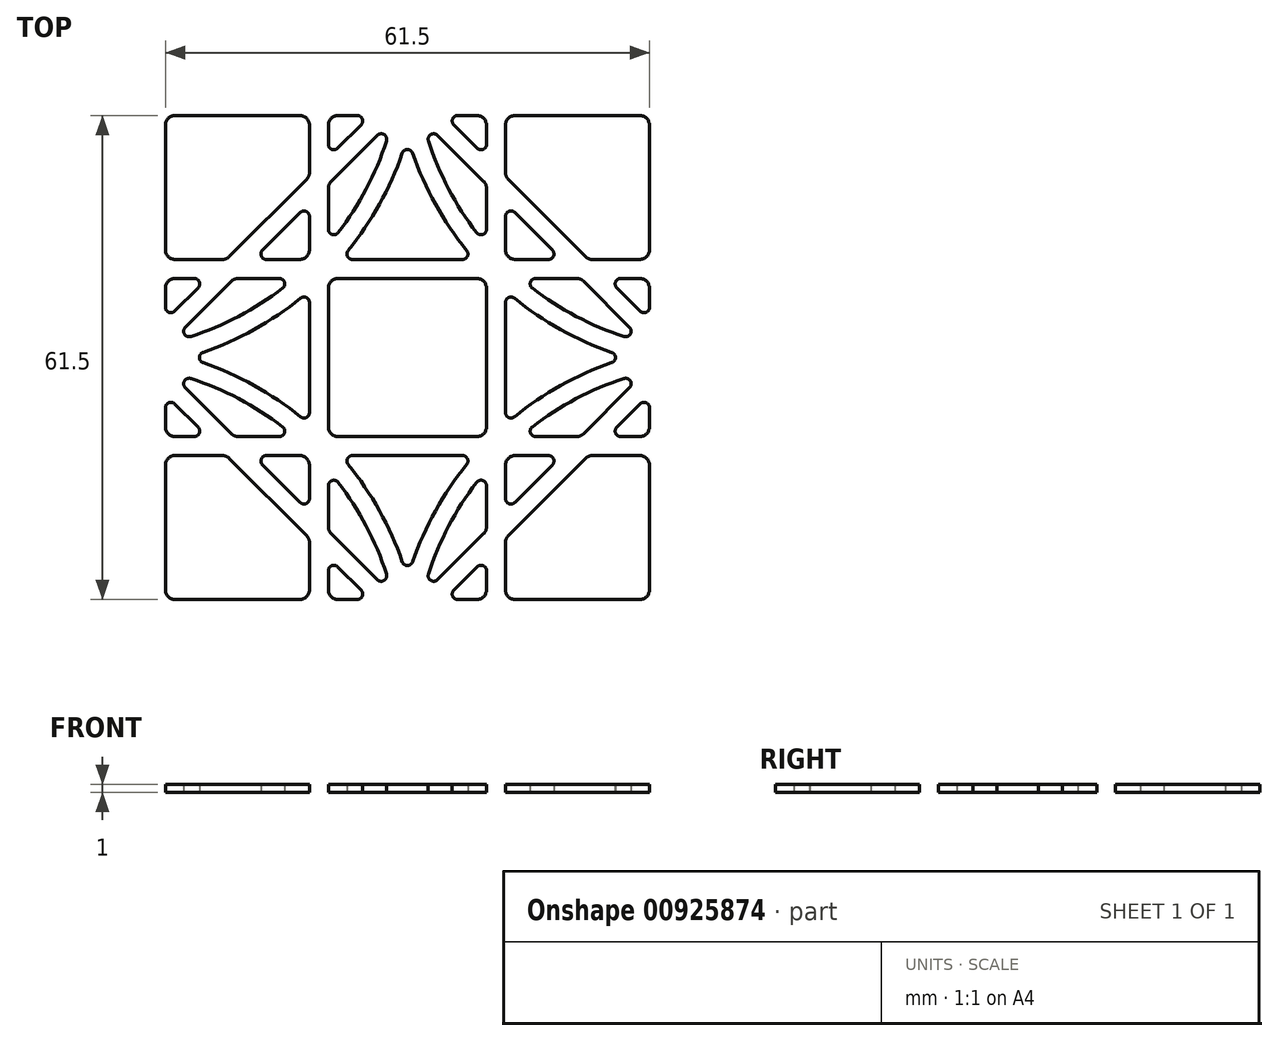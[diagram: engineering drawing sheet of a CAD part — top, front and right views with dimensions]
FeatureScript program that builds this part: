
annotation { "Feature Type Name" : "Feature", "Feature Type Description" : "" }
export const myFeature = defineFeature(function(context is Context, id is Id, definition is map)
    precondition{}
    {
        {
            var Q0;
            Q0=qCreatedBy(makeId("Top.planeOp"),FACE);
            var sketch = newSketch(context, id + "F0", { "sketchPlane" : qUnion([Q0])});
            skLineSegment(sketch, "E0.bottom", {"start": v(33.75, 33.75) * mm, "end": v(-33.75, 33.75) * mm, "construction": true});
            skLineSegment(sketch, "E0.top", {"start": v(33.75, -33.75) * mm, "end": v(-33.75, -33.75) * mm, "construction": true});
            skLineSegment(sketch, "E0.left", {"start": v(33.75, 33.75) * mm, "end": v(33.75, -33.75) * mm, "construction": true});
            skLineSegment(sketch, "E0.right", {"start": v(-33.75, 33.75) * mm, "end": v(-33.75, -33.75) * mm, "construction": true});
            skPoint(sketch, "E0.middle", {"position": v(0, 0) * mm});
            skLineSegment(sketch, "E1", {"start": v(-11.25, 33.75) * mm, "end": v(-11.25, -33.75) * mm, "construction": true});
            skLineSegment(sketch, "E2.1.0", {"start": v(-33.75, -11.25) * mm, "end": v(33.75, -11.25) * mm, "construction": true});
            skLineSegment(sketch, "E2.2.0", {"start": v(11.25, -33.75) * mm, "end": v(11.25, 33.75) * mm, "construction": true});
            skLineSegment(sketch, "E2.3.0", {"start": v(33.75, 11.25) * mm, "end": v(-33.75, 11.25) * mm, "construction": true});
            skArc(sketch, "E3", {"start": v(0, -33.75) * mm, "mid": v(-11.25, -11.25) * mm, "end": v(-33.75, 0) * mm, "construction": true});
            skPoint(sketch, "E4", {"position": v(-11.25, -11.25) * mm});
            skLineSegment(sketch, "E5", {"start": v(-33.75, 0) * mm, "end": v(0, -33.75) * mm, "construction": true});
            skArc(sketch, "E6", {"start": v(33.75, 0) * mm, "mid": v(11.25, -11.25) * mm, "end": v(0, -33.75) * mm, "construction": true});
            skPoint(sketch, "E7", {"position": v(11.25, -11.25) * mm});
            skLineSegment(sketch, "E8.bottom", {"start": v(-29.5, -12.45) * mm, "end": v(-23.51, -12.45) * mm});
            skLineSegment(sketch, "E8.top", {"start": v(-29.5, -30.75) * mm, "end": v(-13.7, -30.75) * mm});
            skLineSegment(sketch, "E8.left", {"start": v(-30.75, -13.7) * mm, "end": v(-30.75, -29.5) * mm});
            skLineSegment(sketch, "E8.right", {"start": v(-12.45, -13.7) * mm, "end": v(-12.45, -17.91) * mm});
            skLineSegment(sketch, "E9.bottom", {"start": v(-6.99, -12.45) * mm, "end": v(6.99, -12.45) * mm});
            skLineSegment(sketch, "E9.top", {"start": v(-8.8, -30.75) * mm, "end": v(-6.39, -30.75) * mm});
            skLineSegment(sketch, "E10.bottom", {"start": v(-8.8, 10.05) * mm, "end": v(8.8, 10.05) * mm});
            skLineSegment(sketch, "E10.top", {"start": v(-8.8, -10.05) * mm, "end": v(8.8, -10.05) * mm});
            skLineSegment(sketch, "E10.left", {"start": v(-10.05, 8.8) * mm, "end": v(-10.05, -8.8) * mm});
            skLineSegment(sketch, "E10.right", {"start": v(10.05, 8.8) * mm, "end": v(10.05, -8.8) * mm});
            skLineSegment(sketch, "E11.0", {"start": v(-22.63, -12.82) * mm, "end": v(-12.82, -22.63) * mm});
            skLineSegment(sketch, "E12.0", {"start": v(-18.4, -13.64) * mm, "end": v(-13.64, -18.4) * mm});
            skLineSegment(sketch, "E13.trimOffspring", {"start": v(-17.91, -12.45) * mm, "end": v(-13.7, -12.45) * mm});
            skLineSegment(sketch, "E14.trimOffspring", {"start": v(-12.45, -23.51) * mm, "end": v(-12.45, -29.5) * mm});
            skLineSegment(sketch, "E15.trimOffspring", {"start": v(-8.86, -26.6) * mm, "end": v(-5.9, -29.56) * mm});
            skLineSegment(sketch, "E16.trimOffspring", {"start": v(-9.68, -22.37) * mm, "end": v(-3.83, -28.22) * mm});
            skArc(sketch, "E17.0", {"start": v(-0.66, -25.95) * mm, "mid": v(-3.56, -19.47) * mm, "end": v(-7.53, -13.6) * mm});
            skArc(sketch, "E18.0", {"start": v(-2.67, -27.51) * mm, "mid": v(-5.23, -21.42) * mm, "end": v(-8.8, -15.86) * mm});
            skArc(sketch, "E19.0", {"start": v(7.53, -13.6) * mm, "mid": v(3.56, -19.47) * mm, "end": v(0.66, -25.95) * mm});
            skLineSegment(sketch, "E20.trimOffspring", {"start": v(-10.05, -16.29) * mm, "end": v(-10.05, -21.49) * mm});
            skLineSegment(sketch, "E21.trimOffspring", {"start": v(-10.05, -27.09) * mm, "end": v(-10.05, -29.5) * mm});
            skPoint(sketch, "E22.visualSharp", {"position": v(-10.05, 10.05) * mm});
            skArc(sketch, "E22.filletArc", {"start": v(-8.8, 10.05) * mm, "mid": v(-9.68, 9.68) * mm, "end": v(-10.05, 8.8) * mm});
            skPoint(sketch, "E23.visualSharp", {"position": v(10.05, 10.05) * mm});
            skArc(sketch, "E23.filletArc", {"start": v(10.05, 8.8) * mm, "mid": v(9.68, 9.68) * mm, "end": v(8.8, 10.05) * mm});
            skPoint(sketch, "E24.visualSharp", {"position": v(10.05, -10.05) * mm});
            skArc(sketch, "E24.filletArc", {"start": v(8.8, -10.05) * mm, "mid": v(9.68, -9.68) * mm, "end": v(10.05, -8.8) * mm});
            skPoint(sketch, "E25.visualSharp", {"position": v(-10.05, -10.05) * mm});
            skArc(sketch, "E25.filletArc", {"start": v(-10.05, -8.8) * mm, "mid": v(-9.68, -9.68) * mm, "end": v(-8.8, -10.05) * mm});
            skPoint(sketch, "E26.visualSharp", {"position": v(-23, -12.45) * mm});
            skArc(sketch, "E26.filletArc", {"start": v(-22.63, -12.82) * mm, "mid": v(-23.04, -12.55) * mm, "end": v(-23.51, -12.45) * mm});
            skPoint(sketch, "E27.visualSharp", {"position": v(-30.75, -12.45) * mm});
            skArc(sketch, "E27.filletArc", {"start": v(-29.5, -12.45) * mm, "mid": v(-30.38, -12.82) * mm, "end": v(-30.75, -13.7) * mm});
            skPoint(sketch, "E28.visualSharp", {"position": v(-30.75, -30.75) * mm});
            skArc(sketch, "E28.filletArc", {"start": v(-30.75, -29.5) * mm, "mid": v(-30.38, -30.38) * mm, "end": v(-29.5, -30.75) * mm});
            skPoint(sketch, "E29.visualSharp", {"position": v(-12.45, -30.75) * mm});
            skArc(sketch, "E29.filletArc", {"start": v(-13.7, -30.75) * mm, "mid": v(-12.82, -30.38) * mm, "end": v(-12.45, -29.5) * mm});
            skPoint(sketch, "E30.visualSharp", {"position": v(-10.05, -30.75) * mm});
            skArc(sketch, "E30.filletArc", {"start": v(-10.05, -29.5) * mm, "mid": v(-9.68, -30.38) * mm, "end": v(-8.8, -30.75) * mm});
            skPoint(sketch, "E31.visualSharp", {"position": v(-12.45, -23) * mm});
            skArc(sketch, "E31.filletArc", {"start": v(-12.45, -23.51) * mm, "mid": v(-12.55, -23.04) * mm, "end": v(-12.82, -22.63) * mm});
            skPoint(sketch, "E32.visualSharp", {"position": v(-12.45, -12.45) * mm});
            skArc(sketch, "E32.filletArc", {"start": v(-12.45, -13.7) * mm, "mid": v(-12.82, -12.82) * mm, "end": v(-13.7, -12.45) * mm});
            skPoint(sketch, "E33.visualSharp", {"position": v(-8.49, -12.45) * mm});
            skArc(sketch, "E33.filletArc", {"start": v(-6.99, -12.45) * mm, "mid": v(-7.62, -12.85) * mm, "end": v(-7.53, -13.6) * mm});
            skPoint(sketch, "E34.visualSharp", {"position": v(8.49, -12.45) * mm});
            skArc(sketch, "E34.filletArc", {"start": v(7.53, -13.6) * mm, "mid": v(7.62, -12.85) * mm, "end": v(6.99, -12.45) * mm});
            skPoint(sketch, "E35.visualSharp", {"position": v(-19.6, -12.45) * mm});
            skArc(sketch, "E35.filletArc", {"start": v(-17.91, -12.45) * mm, "mid": v(-18.56, -12.88) * mm, "end": v(-18.4, -13.64) * mm});
            skPoint(sketch, "E36.visualSharp", {"position": v(-12.45, -19.6) * mm});
            skArc(sketch, "E36.filletArc", {"start": v(-13.64, -18.4) * mm, "mid": v(-12.88, -18.56) * mm, "end": v(-12.45, -17.91) * mm});
            skPoint(sketch, "E37.visualSharp", {"position": v(-10.05, -14.31) * mm});
            skArc(sketch, "E37.filletArc", {"start": v(-8.8, -15.86) * mm, "mid": v(-9.58, -15.63) * mm, "end": v(-10.05, -16.29) * mm});
            skPoint(sketch, "E38.visualSharp", {"position": v(-1.92, -30.13) * mm});
            skArc(sketch, "E38.filletArc", {"start": v(-3.83, -28.22) * mm, "mid": v(-2.97, -28.32) * mm, "end": v(-2.67, -27.51) * mm});
            skPoint(sketch, "E39.visualSharp", {"position": v(0, -28.04) * mm});
            skArc(sketch, "E39.filletArc", {"start": v(-0.66, -25.95) * mm, "mid": v(0, -26.42) * mm, "end": v(0.66, -25.95) * mm});
            skPoint(sketch, "E40.visualSharp", {"position": v(-10.05, -25.4) * mm});
            skArc(sketch, "E40.filletArc", {"start": v(-8.86, -26.6) * mm, "mid": v(-9.62, -26.44) * mm, "end": v(-10.05, -27.09) * mm});
            skPoint(sketch, "E41.visualSharp", {"position": v(-4.7, -30.75) * mm});
            skArc(sketch, "E41.filletArc", {"start": v(-6.39, -30.75) * mm, "mid": v(-5.74, -30.32) * mm, "end": v(-5.9, -29.56) * mm});
            skPoint(sketch, "E42.visualSharp", {"position": v(-10.05, -22) * mm});
            skArc(sketch, "E42.filletArc", {"start": v(-10.05, -21.49) * mm, "mid": v(-9.95, -21.96) * mm, "end": v(-9.68, -22.37) * mm});
            skLineSegment(sketch, "E43", {"start": v(0, 0) * mm, "end": v(0, 17.39) * mm});
            skArc(sketch, "E44.MirrorCS", {"start": v(10.05, -21.49) * mm, "mid": v(9.95, -21.96) * mm, "end": v(9.68, -22.37) * mm});
            skArc(sketch, "E45.MirrorCS", {"start": v(8.86, -26.6) * mm, "mid": v(9.62, -26.44) * mm, "end": v(10.05, -27.09) * mm});
            skArc(sketch, "E46.MirrorCS", {"start": v(10.05, -29.5) * mm, "mid": v(9.68, -30.38) * mm, "end": v(8.8, -30.75) * mm});
            skArc(sketch, "E47.MirrorCS", {"start": v(6.39, -30.75) * mm, "mid": v(5.74, -30.32) * mm, "end": v(5.9, -29.56) * mm});
            skArc(sketch, "E48.MirrorCS", {"start": v(3.83, -28.22) * mm, "mid": v(2.97, -28.32) * mm, "end": v(2.67, -27.51) * mm});
            skLineSegment(sketch, "E49.MirrorCS", {"start": v(8.8, -30.75) * mm, "end": v(6.39, -30.75) * mm});
            skPoint(sketch, "E50.MirrorP", {"position": v(10.05, -22) * mm});
            skArc(sketch, "E51.MirrorCS", {"start": v(2.67, -27.51) * mm, "mid": v(5.23, -21.42) * mm, "end": v(8.8, -15.86) * mm});
            skPoint(sketch, "E52.MirrorP", {"position": v(10.05, -25.4) * mm});
            skLineSegment(sketch, "E53.MirrorCS", {"start": v(10.05, -16.29) * mm, "end": v(10.05, -21.49) * mm});
            skLineSegment(sketch, "E54.MirrorCS", {"start": v(9.68, -22.37) * mm, "end": v(3.83, -28.22) * mm});
            skArc(sketch, "E55.MirrorCS", {"start": v(8.8, -15.86) * mm, "mid": v(9.58, -15.63) * mm, "end": v(10.05, -16.29) * mm});
            skLineSegment(sketch, "E56.MirrorCS", {"start": v(10.05, -27.09) * mm, "end": v(10.05, -29.5) * mm});
            skPoint(sketch, "E57.MirrorP", {"position": v(4.7, -30.75) * mm});
            skPoint(sketch, "E58.MirrorP", {"position": v(10.05, -30.75) * mm});
            skLineSegment(sketch, "E59.MirrorCS", {"start": v(8.86, -26.6) * mm, "end": v(5.9, -29.56) * mm});
            skPoint(sketch, "E60.1.0", {"position": v(12.45, -30.75) * mm});
            skArc(sketch, "E60.1.1", {"start": v(13.6, 7.53) * mm, "mid": v(19.47, 3.56) * mm, "end": v(25.95, 0.66) * mm});
            skPoint(sketch, "E60.1.2", {"position": v(11.25, 11.25) * mm});
            skLineSegment(sketch, "E60.1.3", {"start": v(22.37, -9.68) * mm, "end": v(28.22, -3.83) * mm});
            skLineSegment(sketch, "E60.1.4", {"start": v(12.45, -6.99) * mm, "end": v(12.45, 6.99) * mm});
            skPoint(sketch, "E60.1.5", {"position": v(19.6, -12.45) * mm});
            skLineSegment(sketch, "E60.1.6", {"start": v(22.37, 9.68) * mm, "end": v(28.22, 3.83) * mm});
            skLineSegment(sketch, "E60.1.7", {"start": v(13.64, -18.4) * mm, "end": v(18.4, -13.64) * mm});
            skLineSegment(sketch, "E60.1.8", {"start": v(26.6, -8.86) * mm, "end": v(29.56, -5.9) * mm});
            skPoint(sketch, "E60.1.10", {"position": v(30.75, -30.75) * mm});
            skPoint(sketch, "E60.1.11", {"position": v(28.04, 0) * mm});
            skLineSegment(sketch, "E60.1.12", {"start": v(27.09, -10.05) * mm, "end": v(29.5, -10.05) * mm});
            skArc(sketch, "E60.1.13", {"start": v(27.51, 2.67) * mm, "mid": v(21.42, 5.23) * mm, "end": v(15.86, 8.8) * mm});
            skPoint(sketch, "E60.1.14", {"position": v(12.45, -19.6) * mm});
            skPoint(sketch, "E60.1.15", {"position": v(30.75, -10.05) * mm});
            skArc(sketch, "E60.1.16", {"start": v(25.95, -0.66) * mm, "mid": v(19.47, -3.56) * mm, "end": v(13.6, -7.53) * mm});
            skLineSegment(sketch, "E60.1.17", {"start": v(13.7, -12.45) * mm, "end": v(17.91, -12.45) * mm});
            skArc(sketch, "E60.1.18", {"start": v(27.51, -2.67) * mm, "mid": v(21.42, -5.23) * mm, "end": v(15.86, -8.8) * mm});
            skLineSegment(sketch, "E60.1.19", {"start": v(27.09, 10.05) * mm, "end": v(29.5, 10.05) * mm});
            skLineSegment(sketch, "E60.1.20", {"start": v(23.51, -12.45) * mm, "end": v(29.5, -12.45) * mm});
            skLineSegment(sketch, "E60.1.21", {"start": v(12.45, -17.91) * mm, "end": v(12.45, -13.7) * mm});
            skLineSegment(sketch, "E60.1.22", {"start": v(13.7, -30.75) * mm, "end": v(29.5, -30.75) * mm});
            skPoint(sketch, "E60.1.23", {"position": v(14.31, -10.05) * mm});
            skPoint(sketch, "E60.1.24", {"position": v(22, 10.05) * mm});
            skLineSegment(sketch, "E60.1.25", {"start": v(16.29, 10.05) * mm, "end": v(21.49, 10.05) * mm});
            skPoint(sketch, "E60.1.26", {"position": v(30.13, -1.92) * mm});
            skLineSegment(sketch, "E60.1.27", {"start": v(12.82, -22.63) * mm, "end": v(22.63, -12.82) * mm});
            skLineSegment(sketch, "E60.1.28", {"start": v(16.29, -10.05) * mm, "end": v(21.49, -10.05) * mm});
            skPoint(sketch, "E60.1.29", {"position": v(30.75, -12.45) * mm});
            skPoint(sketch, "E60.1.30", {"position": v(25.4, 10.05) * mm});
            skLineSegment(sketch, "E60.1.31", {"start": v(30.75, -8.8) * mm, "end": v(30.75, -6.39) * mm});
            skLineSegment(sketch, "E60.1.32", {"start": v(30.75, 8.8) * mm, "end": v(30.75, 6.39) * mm});
            skPoint(sketch, "E60.1.33", {"position": v(23, -12.45) * mm});
            skLineSegment(sketch, "E60.1.34", {"start": v(12.45, -29.5) * mm, "end": v(12.45, -23.51) * mm});
            skPoint(sketch, "E60.1.35", {"position": v(25.4, -10.05) * mm});
            skPoint(sketch, "E60.1.36", {"position": v(22, -10.05) * mm});
            skPoint(sketch, "E60.1.37", {"position": v(12.45, -8.49) * mm});
            skPoint(sketch, "E60.1.38", {"position": v(30.75, 4.7) * mm});
            skPoint(sketch, "E60.1.39", {"position": v(12.45, -23) * mm});
            skPoint(sketch, "E60.1.40", {"position": v(30.75, 10.05) * mm});
            skLineSegment(sketch, "E60.1.41", {"start": v(30.75, -29.5) * mm, "end": v(30.75, -13.7) * mm});
            skPoint(sketch, "E60.1.42", {"position": v(30.75, -4.7) * mm});
            skLineSegment(sketch, "E60.1.43", {"start": v(26.6, 8.86) * mm, "end": v(29.56, 5.9) * mm});
            skPoint(sketch, "E60.1.44", {"position": v(12.45, -12.45) * mm});
            skPoint(sketch, "E60.1.45", {"position": v(12.45, 8.49) * mm});
            skArc(sketch, "E60.1.46", {"start": v(13.6, 7.53) * mm, "mid": v(12.85, 7.62) * mm, "end": v(12.45, 6.99) * mm});
            skArc(sketch, "E60.1.47", {"start": v(28.22, -3.83) * mm, "mid": v(28.32, -2.97) * mm, "end": v(27.51, -2.67) * mm});
            skArc(sketch, "E60.1.48", {"start": v(12.45, -6.99) * mm, "mid": v(12.85, -7.62) * mm, "end": v(13.6, -7.53) * mm});
            skArc(sketch, "E60.1.49", {"start": v(29.5, -30.75) * mm, "mid": v(30.38, -30.38) * mm, "end": v(30.75, -29.5) * mm});
            skArc(sketch, "E60.1.50", {"start": v(30.75, -13.7) * mm, "mid": v(30.38, -12.82) * mm, "end": v(29.5, -12.45) * mm});
            skArc(sketch, "E60.1.51", {"start": v(12.45, -29.5) * mm, "mid": v(12.82, -30.38) * mm, "end": v(13.7, -30.75) * mm});
            skArc(sketch, "E60.1.52", {"start": v(30.75, 6.39) * mm, "mid": v(30.32, 5.74) * mm, "end": v(29.56, 5.9) * mm});
            skArc(sketch, "E60.1.53", {"start": v(15.86, -8.8) * mm, "mid": v(15.63, -9.58) * mm, "end": v(16.29, -10.05) * mm});
            skArc(sketch, "E60.1.54", {"start": v(28.22, 3.83) * mm, "mid": v(28.32, 2.97) * mm, "end": v(27.51, 2.67) * mm});
            skArc(sketch, "E60.1.55", {"start": v(12.45, -17.91) * mm, "mid": v(12.88, -18.56) * mm, "end": v(13.64, -18.4) * mm});
            skArc(sketch, "E60.1.56", {"start": v(30.75, -6.39) * mm, "mid": v(30.32, -5.74) * mm, "end": v(29.56, -5.9) * mm});
            skArc(sketch, "E60.1.57", {"start": v(29.5, -10.05) * mm, "mid": v(30.38, -9.68) * mm, "end": v(30.75, -8.8) * mm});
            skArc(sketch, "E60.1.58", {"start": v(26.6, -8.86) * mm, "mid": v(26.44, -9.62) * mm, "end": v(27.09, -10.05) * mm});
            skArc(sketch, "E60.1.59", {"start": v(13.7, -12.45) * mm, "mid": v(12.82, -12.82) * mm, "end": v(12.45, -13.7) * mm});
            skArc(sketch, "E60.1.60", {"start": v(26.6, 8.86) * mm, "mid": v(26.44, 9.62) * mm, "end": v(27.09, 10.05) * mm});
            skArc(sketch, "E60.1.61", {"start": v(18.4, -13.64) * mm, "mid": v(18.56, -12.88) * mm, "end": v(17.91, -12.45) * mm});
            skArc(sketch, "E60.1.62", {"start": v(29.5, 10.05) * mm, "mid": v(30.38, 9.68) * mm, "end": v(30.75, 8.8) * mm});
            skArc(sketch, "E60.1.63", {"start": v(15.86, 8.8) * mm, "mid": v(15.63, 9.58) * mm, "end": v(16.29, 10.05) * mm});
            skArc(sketch, "E60.1.64", {"start": v(25.95, -0.66) * mm, "mid": v(26.42, 0) * mm, "end": v(25.95, 0.66) * mm});
            skArc(sketch, "E60.1.65", {"start": v(12.82, -22.63) * mm, "mid": v(12.55, -23.04) * mm, "end": v(12.45, -23.51) * mm});
            skArc(sketch, "E60.1.66", {"start": v(21.49, -10.05) * mm, "mid": v(21.96, -9.95) * mm, "end": v(22.37, -9.68) * mm});
            skArc(sketch, "E60.1.67", {"start": v(21.49, 10.05) * mm, "mid": v(21.96, 9.95) * mm, "end": v(22.37, 9.68) * mm});
            skArc(sketch, "E60.1.68", {"start": v(23.51, -12.45) * mm, "mid": v(23.04, -12.55) * mm, "end": v(22.63, -12.82) * mm});
            skPoint(sketch, "E60.2.0", {"position": v(30.75, 12.45) * mm});
            skArc(sketch, "E60.2.1", {"start": v(-7.53, 13.6) * mm, "mid": v(-3.56, 19.47) * mm, "end": v(-0.66, 25.95) * mm});
            skPoint(sketch, "E60.2.2", {"position": v(-11.25, 11.25) * mm});
            skLineSegment(sketch, "E60.2.3", {"start": v(9.68, 22.37) * mm, "end": v(3.83, 28.22) * mm});
            skLineSegment(sketch, "E60.2.4", {"start": v(6.99, 12.45) * mm, "end": v(-6.99, 12.45) * mm});
            skPoint(sketch, "E60.2.5", {"position": v(12.45, 19.6) * mm});
            skLineSegment(sketch, "E60.2.6", {"start": v(-9.68, 22.37) * mm, "end": v(-3.83, 28.22) * mm});
            skLineSegment(sketch, "E60.2.7", {"start": v(18.4, 13.64) * mm, "end": v(13.64, 18.4) * mm});
            skLineSegment(sketch, "E60.2.8", {"start": v(8.86, 26.6) * mm, "end": v(5.9, 29.56) * mm});
            skPoint(sketch, "E60.2.9", {"position": v(11.25, 11.25) * mm});
            skPoint(sketch, "E60.2.10", {"position": v(30.75, 30.75) * mm});
            skPoint(sketch, "E60.2.11", {"position": v(0, 28.04) * mm});
            skLineSegment(sketch, "E60.2.12", {"start": v(10.05, 27.09) * mm, "end": v(10.05, 29.5) * mm});
            skArc(sketch, "E60.2.13", {"start": v(-2.67, 27.51) * mm, "mid": v(-5.23, 21.42) * mm, "end": v(-8.8, 15.86) * mm});
            skPoint(sketch, "E60.2.14", {"position": v(19.6, 12.45) * mm});
            skPoint(sketch, "E60.2.15", {"position": v(10.05, 30.75) * mm});
            skArc(sketch, "E60.2.16", {"start": v(0.66, 25.95) * mm, "mid": v(3.56, 19.47) * mm, "end": v(7.53, 13.6) * mm});
            skLineSegment(sketch, "E60.2.17", {"start": v(12.45, 13.7) * mm, "end": v(12.45, 17.91) * mm});
            skArc(sketch, "E60.2.18", {"start": v(2.67, 27.51) * mm, "mid": v(5.23, 21.42) * mm, "end": v(8.8, 15.86) * mm});
            skLineSegment(sketch, "E60.2.19", {"start": v(-10.05, 27.09) * mm, "end": v(-10.05, 29.5) * mm});
            skLineSegment(sketch, "E60.2.20", {"start": v(12.45, 23.51) * mm, "end": v(12.45, 29.5) * mm});
            skLineSegment(sketch, "E60.2.21", {"start": v(17.91, 12.45) * mm, "end": v(13.7, 12.45) * mm});
            skLineSegment(sketch, "E60.2.22", {"start": v(30.75, 13.7) * mm, "end": v(30.75, 29.5) * mm});
            skPoint(sketch, "E60.2.23", {"position": v(10.05, 14.31) * mm});
            skPoint(sketch, "E60.2.24", {"position": v(-10.05, 22) * mm});
            skLineSegment(sketch, "E60.2.25", {"start": v(-10.05, 16.29) * mm, "end": v(-10.05, 21.49) * mm});
            skPoint(sketch, "E60.2.26", {"position": v(1.92, 30.13) * mm});
            skLineSegment(sketch, "E60.2.27", {"start": v(22.63, 12.82) * mm, "end": v(12.82, 22.63) * mm});
            skLineSegment(sketch, "E60.2.28", {"start": v(10.05, 16.29) * mm, "end": v(10.05, 21.49) * mm});
            skPoint(sketch, "E60.2.29", {"position": v(12.45, 30.75) * mm});
            skPoint(sketch, "E60.2.30", {"position": v(-10.05, 25.4) * mm});
            skLineSegment(sketch, "E60.2.31", {"start": v(8.8, 30.75) * mm, "end": v(6.39, 30.75) * mm});
            skLineSegment(sketch, "E60.2.32", {"start": v(-8.8, 30.75) * mm, "end": v(-6.39, 30.75) * mm});
            skPoint(sketch, "E60.2.33", {"position": v(12.45, 23) * mm});
            skLineSegment(sketch, "E60.2.34", {"start": v(29.5, 12.45) * mm, "end": v(23.51, 12.45) * mm});
            skPoint(sketch, "E60.2.35", {"position": v(10.05, 25.4) * mm});
            skPoint(sketch, "E60.2.36", {"position": v(10.05, 22) * mm});
            skPoint(sketch, "E60.2.37", {"position": v(8.49, 12.45) * mm});
            skPoint(sketch, "E60.2.38", {"position": v(-4.7, 30.75) * mm});
            skPoint(sketch, "E60.2.39", {"position": v(23, 12.45) * mm});
            skPoint(sketch, "E60.2.40", {"position": v(-10.05, 30.75) * mm});
            skLineSegment(sketch, "E60.2.41", {"start": v(29.5, 30.75) * mm, "end": v(13.7, 30.75) * mm});
            skPoint(sketch, "E60.2.42", {"position": v(4.7, 30.75) * mm});
            skLineSegment(sketch, "E60.2.43", {"start": v(-8.86, 26.6) * mm, "end": v(-5.9, 29.56) * mm});
            skPoint(sketch, "E60.2.44", {"position": v(12.45, 12.45) * mm});
            skPoint(sketch, "E60.2.45", {"position": v(-8.49, 12.45) * mm});
            skArc(sketch, "E60.2.46", {"start": v(-7.53, 13.6) * mm, "mid": v(-7.62, 12.85) * mm, "end": v(-6.99, 12.45) * mm});
            skArc(sketch, "E60.2.47", {"start": v(3.83, 28.22) * mm, "mid": v(2.97, 28.32) * mm, "end": v(2.67, 27.51) * mm});
            skArc(sketch, "E60.2.48", {"start": v(6.99, 12.45) * mm, "mid": v(7.62, 12.85) * mm, "end": v(7.53, 13.6) * mm});
            skArc(sketch, "E60.2.49", {"start": v(30.75, 29.5) * mm, "mid": v(30.38, 30.38) * mm, "end": v(29.5, 30.75) * mm});
            skArc(sketch, "E60.2.50", {"start": v(13.7, 30.75) * mm, "mid": v(12.82, 30.38) * mm, "end": v(12.45, 29.5) * mm});
            skArc(sketch, "E60.2.51", {"start": v(29.5, 12.45) * mm, "mid": v(30.38, 12.82) * mm, "end": v(30.75, 13.7) * mm});
            skArc(sketch, "E60.2.52", {"start": v(-6.39, 30.75) * mm, "mid": v(-5.74, 30.32) * mm, "end": v(-5.9, 29.56) * mm});
            skArc(sketch, "E60.2.53", {"start": v(8.8, 15.86) * mm, "mid": v(9.58, 15.63) * mm, "end": v(10.05, 16.29) * mm});
            skArc(sketch, "E60.2.54", {"start": v(-3.83, 28.22) * mm, "mid": v(-2.97, 28.32) * mm, "end": v(-2.67, 27.51) * mm});
            skArc(sketch, "E60.2.55", {"start": v(17.91, 12.45) * mm, "mid": v(18.56, 12.88) * mm, "end": v(18.4, 13.64) * mm});
            skArc(sketch, "E60.2.56", {"start": v(6.39, 30.75) * mm, "mid": v(5.74, 30.32) * mm, "end": v(5.9, 29.56) * mm});
            skArc(sketch, "E60.2.57", {"start": v(10.05, 29.5) * mm, "mid": v(9.68, 30.38) * mm, "end": v(8.8, 30.75) * mm});
            skArc(sketch, "E60.2.58", {"start": v(8.86, 26.6) * mm, "mid": v(9.62, 26.44) * mm, "end": v(10.05, 27.09) * mm});
            skArc(sketch, "E60.2.59", {"start": v(12.45, 13.7) * mm, "mid": v(12.82, 12.82) * mm, "end": v(13.7, 12.45) * mm});
            skArc(sketch, "E60.2.60", {"start": v(-8.86, 26.6) * mm, "mid": v(-9.62, 26.44) * mm, "end": v(-10.05, 27.09) * mm});
            skArc(sketch, "E60.2.61", {"start": v(13.64, 18.4) * mm, "mid": v(12.88, 18.56) * mm, "end": v(12.45, 17.91) * mm});
            skArc(sketch, "E60.2.62", {"start": v(-10.05, 29.5) * mm, "mid": v(-9.68, 30.38) * mm, "end": v(-8.8, 30.75) * mm});
            skArc(sketch, "E60.2.63", {"start": v(-8.8, 15.86) * mm, "mid": v(-9.58, 15.63) * mm, "end": v(-10.05, 16.29) * mm});
            skArc(sketch, "E60.2.64", {"start": v(0.66, 25.95) * mm, "mid": v(0, 26.42) * mm, "end": v(-0.66, 25.95) * mm});
            skArc(sketch, "E60.2.65", {"start": v(22.63, 12.82) * mm, "mid": v(23.04, 12.55) * mm, "end": v(23.51, 12.45) * mm});
            skArc(sketch, "E60.2.66", {"start": v(10.05, 21.49) * mm, "mid": v(9.95, 21.96) * mm, "end": v(9.68, 22.37) * mm});
            skArc(sketch, "E60.2.67", {"start": v(-10.05, 21.49) * mm, "mid": v(-9.95, 21.96) * mm, "end": v(-9.68, 22.37) * mm});
            skArc(sketch, "E60.2.68", {"start": v(12.45, 23.51) * mm, "mid": v(12.55, 23.04) * mm, "end": v(12.82, 22.63) * mm});
            skPoint(sketch, "E60.3.0", {"position": v(-12.45, 30.75) * mm});
            skArc(sketch, "E60.3.1", {"start": v(-13.6, -7.53) * mm, "mid": v(-19.47, -3.56) * mm, "end": v(-25.95, -0.66) * mm});
            skLineSegment(sketch, "E60.3.3", {"start": v(-22.37, 9.68) * mm, "end": v(-28.22, 3.83) * mm});
            skLineSegment(sketch, "E60.3.4", {"start": v(-12.45, 6.99) * mm, "end": v(-12.45, -6.99) * mm});
            skPoint(sketch, "E60.3.5", {"position": v(-19.6, 12.45) * mm});
            skLineSegment(sketch, "E60.3.6", {"start": v(-22.37, -9.68) * mm, "end": v(-28.22, -3.83) * mm});
            skLineSegment(sketch, "E60.3.7", {"start": v(-13.64, 18.4) * mm, "end": v(-18.4, 13.64) * mm});
            skLineSegment(sketch, "E60.3.8", {"start": v(-26.6, 8.86) * mm, "end": v(-29.56, 5.9) * mm});
            skPoint(sketch, "E60.3.9", {"position": v(-11.25, 11.25) * mm});
            skPoint(sketch, "E60.3.10", {"position": v(-30.75, 30.75) * mm});
            skPoint(sketch, "E60.3.11", {"position": v(-28.04, 0) * mm});
            skLineSegment(sketch, "E60.3.12", {"start": v(-27.09, 10.05) * mm, "end": v(-29.5, 10.05) * mm});
            skArc(sketch, "E60.3.13", {"start": v(-27.51, -2.67) * mm, "mid": v(-21.42, -5.23) * mm, "end": v(-15.86, -8.8) * mm});
            skPoint(sketch, "E60.3.14", {"position": v(-12.45, 19.6) * mm});
            skPoint(sketch, "E60.3.15", {"position": v(-30.75, 10.05) * mm});
            skArc(sketch, "E60.3.16", {"start": v(-25.95, 0.66) * mm, "mid": v(-19.47, 3.56) * mm, "end": v(-13.6, 7.53) * mm});
            skLineSegment(sketch, "E60.3.17", {"start": v(-13.7, 12.45) * mm, "end": v(-17.91, 12.45) * mm});
            skArc(sketch, "E60.3.18", {"start": v(-27.51, 2.67) * mm, "mid": v(-21.42, 5.23) * mm, "end": v(-15.86, 8.8) * mm});
            skLineSegment(sketch, "E60.3.19", {"start": v(-27.09, -10.05) * mm, "end": v(-29.5, -10.05) * mm});
            skLineSegment(sketch, "E60.3.20", {"start": v(-23.51, 12.45) * mm, "end": v(-29.5, 12.45) * mm});
            skLineSegment(sketch, "E60.3.21", {"start": v(-12.45, 17.91) * mm, "end": v(-12.45, 13.7) * mm});
            skLineSegment(sketch, "E60.3.22", {"start": v(-13.7, 30.75) * mm, "end": v(-29.5, 30.75) * mm});
            skPoint(sketch, "E60.3.23", {"position": v(-14.31, 10.05) * mm});
            skPoint(sketch, "E60.3.24", {"position": v(-22, -10.05) * mm});
            skLineSegment(sketch, "E60.3.25", {"start": v(-16.29, -10.05) * mm, "end": v(-21.49, -10.05) * mm});
            skPoint(sketch, "E60.3.26", {"position": v(-30.13, 1.92) * mm});
            skLineSegment(sketch, "E60.3.27", {"start": v(-12.82, 22.63) * mm, "end": v(-22.63, 12.82) * mm});
            skLineSegment(sketch, "E60.3.28", {"start": v(-16.29, 10.05) * mm, "end": v(-21.49, 10.05) * mm});
            skPoint(sketch, "E60.3.29", {"position": v(-30.75, 12.45) * mm});
            skPoint(sketch, "E60.3.30", {"position": v(-25.4, -10.05) * mm});
            skLineSegment(sketch, "E60.3.31", {"start": v(-30.75, 8.8) * mm, "end": v(-30.75, 6.39) * mm});
            skLineSegment(sketch, "E60.3.32", {"start": v(-30.75, -8.8) * mm, "end": v(-30.75, -6.39) * mm});
            skPoint(sketch, "E60.3.33", {"position": v(-23, 12.45) * mm});
            skLineSegment(sketch, "E60.3.34", {"start": v(-12.45, 29.5) * mm, "end": v(-12.45, 23.51) * mm});
            skPoint(sketch, "E60.3.35", {"position": v(-25.4, 10.05) * mm});
            skPoint(sketch, "E60.3.36", {"position": v(-22, 10.05) * mm});
            skPoint(sketch, "E60.3.37", {"position": v(-12.45, 8.49) * mm});
            skPoint(sketch, "E60.3.38", {"position": v(-30.75, -4.7) * mm});
            skPoint(sketch, "E60.3.39", {"position": v(-12.45, 23) * mm});
            skPoint(sketch, "E60.3.40", {"position": v(-30.75, -10.05) * mm});
            skLineSegment(sketch, "E60.3.41", {"start": v(-30.75, 29.5) * mm, "end": v(-30.75, 13.7) * mm});
            skPoint(sketch, "E60.3.42", {"position": v(-30.75, 4.7) * mm});
            skLineSegment(sketch, "E60.3.43", {"start": v(-26.6, -8.86) * mm, "end": v(-29.56, -5.9) * mm});
            skPoint(sketch, "E60.3.44", {"position": v(-12.45, 12.45) * mm});
            skPoint(sketch, "E60.3.45", {"position": v(-12.45, -8.49) * mm});
            skArc(sketch, "E60.3.46", {"start": v(-13.6, -7.53) * mm, "mid": v(-12.85, -7.62) * mm, "end": v(-12.45, -6.99) * mm});
            skArc(sketch, "E60.3.47", {"start": v(-28.22, 3.83) * mm, "mid": v(-28.32, 2.97) * mm, "end": v(-27.51, 2.67) * mm});
            skArc(sketch, "E60.3.48", {"start": v(-12.45, 6.99) * mm, "mid": v(-12.85, 7.62) * mm, "end": v(-13.6, 7.53) * mm});
            skArc(sketch, "E60.3.49", {"start": v(-29.5, 30.75) * mm, "mid": v(-30.38, 30.38) * mm, "end": v(-30.75, 29.5) * mm});
            skArc(sketch, "E60.3.50", {"start": v(-30.75, 13.7) * mm, "mid": v(-30.38, 12.82) * mm, "end": v(-29.5, 12.45) * mm});
            skArc(sketch, "E60.3.51", {"start": v(-12.45, 29.5) * mm, "mid": v(-12.82, 30.38) * mm, "end": v(-13.7, 30.75) * mm});
            skArc(sketch, "E60.3.52", {"start": v(-30.75, -6.39) * mm, "mid": v(-30.32, -5.74) * mm, "end": v(-29.56, -5.9) * mm});
            skArc(sketch, "E60.3.53", {"start": v(-15.86, 8.8) * mm, "mid": v(-15.63, 9.58) * mm, "end": v(-16.29, 10.05) * mm});
            skArc(sketch, "E60.3.54", {"start": v(-28.22, -3.83) * mm, "mid": v(-28.32, -2.97) * mm, "end": v(-27.51, -2.67) * mm});
            skArc(sketch, "E60.3.55", {"start": v(-12.45, 17.91) * mm, "mid": v(-12.88, 18.56) * mm, "end": v(-13.64, 18.4) * mm});
            skArc(sketch, "E60.3.56", {"start": v(-30.75, 6.39) * mm, "mid": v(-30.32, 5.74) * mm, "end": v(-29.56, 5.9) * mm});
            skArc(sketch, "E60.3.57", {"start": v(-29.5, 10.05) * mm, "mid": v(-30.38, 9.68) * mm, "end": v(-30.75, 8.8) * mm});
            skArc(sketch, "E60.3.58", {"start": v(-26.6, 8.86) * mm, "mid": v(-26.44, 9.62) * mm, "end": v(-27.09, 10.05) * mm});
            skArc(sketch, "E60.3.59", {"start": v(-13.7, 12.45) * mm, "mid": v(-12.82, 12.82) * mm, "end": v(-12.45, 13.7) * mm});
            skArc(sketch, "E60.3.60", {"start": v(-26.6, -8.86) * mm, "mid": v(-26.44, -9.62) * mm, "end": v(-27.09, -10.05) * mm});
            skArc(sketch, "E60.3.61", {"start": v(-18.4, 13.64) * mm, "mid": v(-18.56, 12.88) * mm, "end": v(-17.91, 12.45) * mm});
            skArc(sketch, "E60.3.62", {"start": v(-29.5, -10.05) * mm, "mid": v(-30.38, -9.68) * mm, "end": v(-30.75, -8.8) * mm});
            skArc(sketch, "E60.3.63", {"start": v(-15.86, -8.8) * mm, "mid": v(-15.63, -9.58) * mm, "end": v(-16.29, -10.05) * mm});
            skArc(sketch, "E60.3.64", {"start": v(-25.95, 0.66) * mm, "mid": v(-26.42, 0) * mm, "end": v(-25.95, -0.66) * mm});
            skArc(sketch, "E60.3.65", {"start": v(-12.82, 22.63) * mm, "mid": v(-12.55, 23.04) * mm, "end": v(-12.45, 23.51) * mm});
            skArc(sketch, "E60.3.66", {"start": v(-21.49, 10.05) * mm, "mid": v(-21.96, 9.95) * mm, "end": v(-22.37, 9.68) * mm});
            skArc(sketch, "E60.3.67", {"start": v(-21.49, -10.05) * mm, "mid": v(-21.96, -9.95) * mm, "end": v(-22.37, -9.68) * mm});
            skArc(sketch, "E60.3.68", {"start": v(-23.51, 12.45) * mm, "mid": v(-23.04, 12.55) * mm, "end": v(-22.63, 12.82) * mm});
            skSolve(sketch);
        }
        {
            var Q0;
            Q0 = qSketchRegion(id + "F0", true);
            extrude(context, id + "F1", {"entities" : qUnion([Q0]), "depth" : 1 * mm, "offsetDistance" : 25 * mm});
        }
    });
